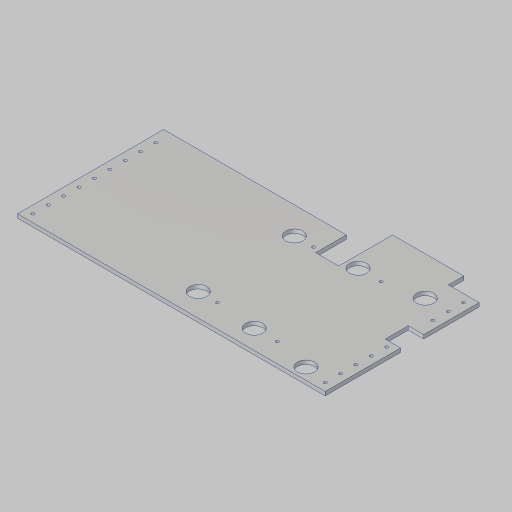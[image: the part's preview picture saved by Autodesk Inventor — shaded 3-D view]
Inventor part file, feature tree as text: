
AUTODESK INVENTOR PART (.ipt)
format: ipt  version: 2023.5 (Build 275446000, 446)  size: 211,456 bytes
history: native  units: in
note: dims shown in document units (in); Inventor stores cm internally (conversion verified against a paired STEP export)
features: sketch x4, extrude x3, hole x2, projected_geometry x2
ambient origin geometry x8: Origin, YZ Plane, XZ Plane, XY Plane, X Axis, Y Axis, Z Axis, Center Point
bodies: Solid1 (feature_tree)
feature tree (11):
  extrude  "Extrusion1"  Depth=11.0in
  hole  "Hole1"  [1 undecoded]
  extrude  "Extrusion2"  Depth=0.5in
  sketch  "Sketch4"  dims[d7=4.3307in d9=1.0in d10=0.3937in d12=1.0in d14=0.201in d15=0.38in d16=0.385in d17=0.25in d18=0.5635in d19=1.0in d20=0.8108in d24=1.0in d25=0.0in d28=4.5in d29=12.0in d30=1.0in d31=2.0in d32=1.125in d33=4.0in d34=2.5in d35=3.25in d36=0.125in d37=3.8976in d38=0.75in d39=1.0in d40=0.0in d42=8.125in d43=1.5in d44=3.5in d45=6.625in d46=1.0in d47=1.5in d48=4.9in d49=2.0in d50=0.125in d51=3.8976in d55=1.5in d57=0.201in d58=0.75in d59=0.385in d60=0.25in d61=0.5635in d62=1.0in d63=0.8108in d64=0.5in d65=0.25in d67=1.25in]
  extrude  "Extrusion3"  Depth=1.0in TaperAngle=0.0deg
  hole  "Hole2"  [1 undecoded]
  sketch  "Sketch1"  dims[d0=20.0in d1=11.0in]
  sketch  "Sketch2"  dims[d2=0.25in d3=0.0in d4=0.5in]
  sketch  "Sketch3"  dims[d5=0.5in d6=0.5in]
  projected_geometry  "Projected Loop1"
  projected_geometry  "Projected Loop2"
note: 2 required parameter values undecoded (feature->parameter linkage not recoverable at this tier; creation-order binding heuristic only, values carry confidence <= 0.55)
